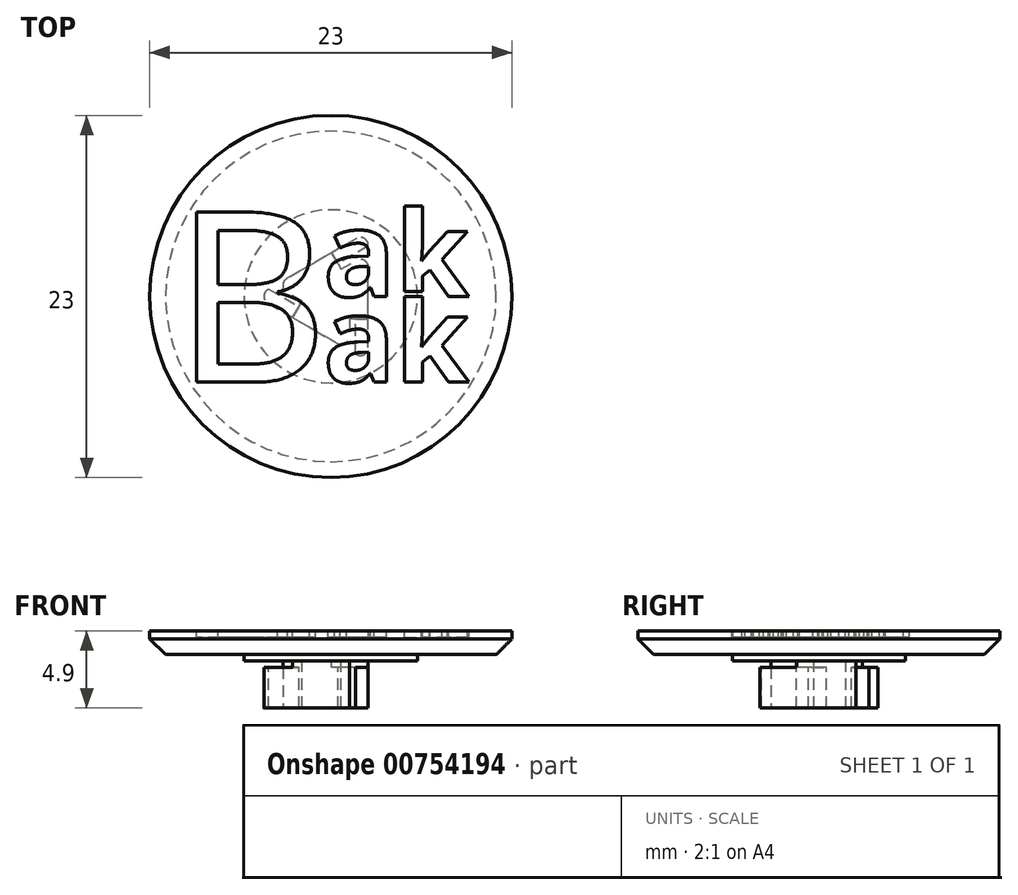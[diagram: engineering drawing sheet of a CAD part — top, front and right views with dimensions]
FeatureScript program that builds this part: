
annotation { "Feature Type Name" : "Feature", "Feature Type Description" : "" }
export const myFeature = defineFeature(function(context is Context, id is Id, definition is map)
    precondition{}
    {
        {
            var Q0;
            Q0=qCreatedBy(makeId("Front.planeOp"),FACE);
            var sketch = newSketch(context, id + "F0", { "sketchPlane" : qUnion([Q0])});
            skLineSegment(sketch, "E0", {"start": v(-4, 5.4) * mm, "end": v(-4, 1.9) * mm});
            skLineSegment(sketch, "E1", {"start": v(-4, 1.9) * mm, "end": v(-5.5, 1.9) * mm});
            skLineSegment(sketch, "E2", {"start": v(-5.5, 1.9) * mm, "end": v(-5.5, 1.5) * mm});
            skLineSegment(sketch, "E3", {"start": v(-5.5, 1.5) * mm, "end": v(-10.5, 1.5) * mm});
            skLineSegment(sketch, "E4", {"start": v(-10.5, 1.5) * mm, "end": v(-11.5, 0.5) * mm});
            skLineSegment(sketch, "E5", {"start": v(-11.5, 0.5) * mm, "end": v(-11.5, 0) * mm});
            skLineSegment(sketch, "E6", {"start": v(-11.5, 0) * mm, "end": v(0, 0) * mm});
            skLineSegment(sketch, "E7", {"start": v(0, 0) * mm, "end": v(0, 5.4) * mm});
            skLineSegment(sketch, "E8", {"start": v(0, 5.4) * mm, "end": v(-4, 5.4) * mm});
            skSolve(sketch);
        }
        {
            var Q0;
            Q0=makeQuery(id+"F0.imprint","IMPRINT",FACE,{"disambiguationData":[TD([[makeQuery(id+"F0.imprint","IMPRINT",EDGE,{"derivedFrom":sQuery(id+"F0.wireOp",EDGE,"E0")}),1.0]])]});
            var Q1;
            Q1=sQuery(id+"F0.wireOp",EDGE,"E7");
            revolve(context, id + "F1", {"surfaceOperationType" : NewSurfaceOperationType.NEW, "entities" : qUnion([Q0]), "axis" : qUnion([Q1]), "revolveType" : RevolveType.FULL});
        }
        {
            var Q0;
            Q0=makeQuery(id+"F1.opRevolve","SWEPT_FACE",FACE,{"disambiguationData":[OSD([sQuery(id+"F0.wireOp",EDGE,"E8")])]});
            var sketch = newSketch(context, id + "F2", { "sketchPlane" : qUnion([Q0])});
            skCircle(sketch, "E9.cCircle", {"center": v(0, 0) * mm, "radius": 4 * mm, "construction": true});
            skLineSegment(sketch, "E9.0", {"start": v(0, 4) * mm, "end": v(4, 0) * mm});
            skLineSegment(sketch, "E9.1", {"start": v(4, 0) * mm, "end": v(0, -4) * mm});
            skLineSegment(sketch, "E9.2", {"start": v(0, -4) * mm, "end": v(-4, 0) * mm});
            skLineSegment(sketch, "E9.3", {"start": v(-4, 0) * mm, "end": v(0, 4) * mm});
            skSolve(sketch);
        }
        {
            var Q0;
            {var subQ0=sQuery(id+"F2.wireOp",EDGE,"E9.3");Q0=makeQuery(id+"F2.imprint","IMPRINT",FACE,{"disambiguationData":[TD([[makeQuery(id+"F2.imprint","IMPRINT",EDGE,{"derivedFrom":subQ0}),1.0]])]});}
            var Q1;
            {var subQ0=sQuery(id+"F2.wireOp",EDGE,"E9.2");Q1=makeQuery(id+"F2.imprint","IMPRINT",FACE,{"disambiguationData":[TD([[makeQuery(id+"F2.imprint","IMPRINT",EDGE,{"derivedFrom":subQ0}),1.0]])]});}
            var Q2;
            {var subQ0=sQuery(id+"F2.wireOp",EDGE,"E9.1");Q2=makeQuery(id+"F2.imprint","IMPRINT",FACE,{"disambiguationData":[TD([[makeQuery(id+"F2.imprint","IMPRINT",EDGE,{"derivedFrom":subQ0}),1.0]])]});}
            var Q3;
            {var subQ0=sQuery(id+"F2.wireOp",EDGE,"E9.0");Q3=makeQuery(id+"F2.imprint","IMPRINT",FACE,{"disambiguationData":[TD([[makeQuery(id+"F2.imprint","IMPRINT",EDGE,{"derivedFrom":subQ0}),1.0]])]});}
            var Q4;
            Q4=makeQuery(id+"F1.opRevolve","SWEPT_FACE",FACE,{"disambiguationData":[OSD([sQuery(id+"F0.wireOp",EDGE,"E1")])]});
            extrude(context, id + "F3", {"entities" : qUnion([Q0, Q1, Q2, Q3]), "operationType" : NewBodyOperationType.REMOVE, "endBound" : BoundingType.UP_TO_SURFACE, "oppositeDirection" : true, "depth" : 25 * mm, "endBoundEntityFace" : qUnion([Q4]), "offsetDistance" : 25 * mm});
        }
        {
            var Q0;
            Q0=qCreatedBy(makeId("Top.planeOp"),FACE);
            var sketch = newSketch(context, id + "F4", { "sketchPlane" : qUnion([Q0])});
            skLineSegment(sketch, "E10", {"start": v(0, 61.35) * mm, "end": v(0, -45.77) * mm});
            skSolve(sketch);
        }
        {
            var Q0;
            Q0=makeQuery(id+"F1.opRevolve","SWEPT_BODY",BODY,{"disambiguationData":[OSD([sQuery(id+"F0.wireOp",EDGE,"E0"),sQuery(id+"F0.wireOp",EDGE,"E1"),sQuery(id+"F0.wireOp",EDGE,"E2"),sQuery(id+"F0.wireOp",EDGE,"E3"),sQuery(id+"F0.wireOp",EDGE,"E4"),sQuery(id+"F0.wireOp",EDGE,"E5"),sQuery(id+"F0.wireOp",EDGE,"E6"),sQuery(id+"F0.wireOp",EDGE,"E7"),sQuery(id+"F0.wireOp",EDGE,"E8")])]});
            var Q1;
            Q1=sQuery(id+"F4.wireOp",EDGE,"E10");
            transform(context, id + "F5", {"entities" : qUnion([Q0]), "transformType" : TransformType.ROTATION, "transformAxis" : qUnion([Q1]), "angle" : 180 * degree, "makeCopy" : false});
        }
        {
            var Q0;
            Q0=makeQuery(id+"F1.opRevolve","SWEPT_FACE",FACE,{"disambiguationData":[OSD([sQuery(id+"F0.wireOp",EDGE,"E6")])]});
            var sketch = newSketch(context, id + "F6", { "sketchPlane" : qUnion([Q0])});
            skLineSegment(sketch, "E11.bottom", {"start": v(-11.93, 11.93) * mm, "end": v(11.93, 11.93) * mm, "construction": true});
            skLineSegment(sketch, "E11.top", {"start": v(-11.93, -11.93) * mm, "end": v(11.93, -11.93) * mm, "construction": true});
            skLineSegment(sketch, "E11.left", {"start": v(-11.93, 11.93) * mm, "end": v(-11.93, -11.93) * mm, "construction": true});
            skLineSegment(sketch, "E11.right", {"start": v(11.93, 11.93) * mm, "end": v(11.93, -11.93) * mm, "construction": true});
            skLineSegment(sketch, "E12", {"start": v(-11.93, 11.93) * mm, "end": v(11.93, -11.93) * mm, "construction": true});
            skLineSegment(sketch, "E13", {"start": v(11.93, 11.93) * mm, "end": v(-11.93, -11.93) * mm, "construction": true});
            skText(sketch, "E14", { "text": "B\n", "fontName": "NotoSans-Regular.ttf"});
            skText(sketch, "E15", { "text": "ak", "fontName": "OpenSans-Bold.ttf"});
            skText(sketch, "E16", { "text": "ak", "fontName": "OpenSans-Bold.ttf"});
            const initialGuessF6  = {"E14": [-0.01, -0.00545, 1, 0, 0.0109], "E15": [-0.00048, 0, 1, 0, 0.00545], "E16": [-0.00048, -0.00545, 1, 0, 0.00545]};
            skSetInitialGuess(sketch, initialGuessF6);
            skSolve(sketch);
        }
        {
            var Q0;
            Q0=makeQuery(id+"F6.imprint","IMPRINT",FACE,{"disambiguationData":[TD([[makeQuery(id+"F6.imprint","IMPRINT",EDGE,{"derivedFrom":sQuery(id+"F6.wireOp",EDGE,"E14.sketch_text.stroke-0")}),-1.0]])]});
            var Q1;
            Q1=makeQuery(id+"F6.imprint","IMPRINT",FACE,{"disambiguationData":[TD([[makeQuery(id+"F6.imprint","IMPRINT",EDGE,{"derivedFrom":sQuery(id+"F6.wireOp",EDGE,"E15.sketch_text.stroke-0")}),-1.0]])]});
            var Q2;
            Q2=makeQuery(id+"F6.imprint","IMPRINT",FACE,{"disambiguationData":[TD([[makeQuery(id+"F6.imprint","IMPRINT",EDGE,{"derivedFrom":sQuery(id+"F6.wireOp",EDGE,"E15.sketch_text.stroke-25")}),-1.0]])]});
            var Q3;
            {var subQ0=sQuery(id+"F6.wireOp",EDGE,"E15.sketch_text.stroke-34");Q3=makeQuery(id+"F6.imprint","IMPRINT",FACE,{"disambiguationData":[TD([[makeQuery(id+"F6.imprint","IMPRINT",EDGE,{"derivedFrom":subQ0}),1.0]])]});}
            var Q4;
            Q4=makeQuery(id+"F6.imprint","IMPRINT",FACE,{"disambiguationData":[TD([[makeQuery(id+"F6.imprint","IMPRINT",EDGE,{"derivedFrom":sQuery(id+"F6.wireOp",EDGE,"E16.sketch_text.stroke-0")}),-1.0]])]});
            extrude(context, id + "F7", {"entities" : qUnion([Q0, Q1, Q2, Q3, Q4]), "operationType" : NewBodyOperationType.REMOVE, "oppositeDirection" : true, "depth" : .4 * mm, "offsetDistance" : 25 * mm});
        }
        {
            var Q0;
            Q0=makeQuery(id+"F1.opRevolve","SWEPT_FACE",FACE,{"disambiguationData":[OSD([sQuery(id+"F0.wireOp",EDGE,"E8")])]});
            var Q1;
            {var subQ0=sQuery(id+"F0.wireOp",EDGE,"E1");Q1=makeQuery(id+"F3.boolean.opBoolean","MERGE",FACE,{"derivedFrom":[makeQuery(id+"F1.opRevolve","SWEPT_FACE",FACE,{"disambiguationData":[OSD([subQ0])]}),makeQuery(id+"F3.opExtrude","CAP_FACE",FACE,{"disambiguationData":[OSD([subQ0]),OD(0.0)],"isStart":false}),makeQuery(id+"F3.opExtrude","CAP_FACE",FACE,{"disambiguationData":[OSD([subQ0]),OD(1.0)],"isStart":false}),makeQuery(id+"F3.opExtrude","CAP_FACE",FACE,{"disambiguationData":[OSD([subQ0]),OD(2.0)],"isStart":false}),makeQuery(id+"F3.opExtrude","CAP_FACE",FACE,{"disambiguationData":[OSD([subQ0]),OD(3.0)],"isStart":false})]});}
            extrude(context, id + "F8", {"entities" : qUnion([Q0]), "operationType" : NewBodyOperationType.REMOVE, "endBound" : BoundingType.UP_TO_SURFACE, "oppositeDirection" : true, "depth" : 25 * mm, "endBoundEntityFace" : qUnion([Q1]), "offsetDistance" : 25 * mm});
        }
        {
            var Q0;
            {var subQ0=sQuery(id+"F0.wireOp",EDGE,"E1");Q0=makeQuery(id+"F8.boolean.opBoolean","MERGE",FACE,{"derivedFrom":[makeQuery(id+"F3.boolean.opBoolean","MERGE",FACE,{"derivedFrom":[makeQuery(id+"F1.opRevolve","SWEPT_FACE",FACE,{"disambiguationData":[OSD([subQ0])]}),makeQuery(id+"F3.opExtrude","CAP_FACE",FACE,{"disambiguationData":[OSD([subQ0]),OD(0.0)],"isStart":false}),makeQuery(id+"F3.opExtrude","CAP_FACE",FACE,{"disambiguationData":[OSD([subQ0]),OD(1.0)],"isStart":false}),makeQuery(id+"F3.opExtrude","CAP_FACE",FACE,{"disambiguationData":[OSD([subQ0]),OD(2.0)],"isStart":false}),makeQuery(id+"F3.opExtrude","CAP_FACE",FACE,{"disambiguationData":[OSD([subQ0]),OD(3.0)],"isStart":false})]}),makeQuery(id+"F8.opExtrude","CAP_FACE",FACE,{"disambiguationData":[OSD([subQ0])],"isStart":false})]});}
            var sketch = newSketch(context, id + "F9", { "sketchPlane" : qUnion([Q0])});
            skCircle(sketch, "E17.cCircle", {"center": v(0, 0) * mm, "radius": 4.75 * mm, "construction": true});
            skLineSegment(sketch, "E17.0", {"start": v(-4.75, 0) * mm, "end": v(2.37, 4.11) * mm});
            skLineSegment(sketch, "E17.1", {"start": v(2.37, 4.11) * mm, "end": v(2.37, -4.11) * mm});
            skLineSegment(sketch, "E17.2", {"start": v(2.38, -4.11) * mm, "end": v(-4.75, 0) * mm});
            skLineSegment(sketch, "E18", {"start": v(1.57, 3.65) * mm, "end": v(1.57, 1.42) * mm});
            skLineSegment(sketch, "E19", {"start": v(1.57, 1.42) * mm, "end": v(1.17, 1.42) * mm});
            skLineSegment(sketch, "E20", {"start": v(1.17, 1.42) * mm, "end": v(1.17, 3.42) * mm});
            skLineSegment(sketch, "E21.1.0", {"start": v(-1.82, 0.3) * mm, "end": v(-3.55, -0.7) * mm});
            skLineSegment(sketch, "E21.1.1", {"start": v(-2.02, 0.65) * mm, "end": v(-1.82, 0.3) * mm});
            skLineSegment(sketch, "E21.1.2", {"start": v(-3.95, -0.46) * mm, "end": v(-2.02, 0.65) * mm});
            skLineSegment(sketch, "E21.2.0", {"start": v(0.64, -1.73) * mm, "end": v(2.37, -2.73) * mm});
            skLineSegment(sketch, "E21.2.1", {"start": v(0.44, -2.07) * mm, "end": v(0.64, -1.73) * mm});
            skLineSegment(sketch, "E21.2.2", {"start": v(2.38, -3.19) * mm, "end": v(0.44, -2.07) * mm});
            skSolve(sketch);
        }
        {
            var Q0;
            {var subQ1=sQuery(id+"F9.wireOp",EDGE,"E18");Q0=makeQuery(id+"F9.imprint","IMPRINT",FACE,{"disambiguationData":[TD([[makeQuery(id+"F9.imprint","IMPRINT",EDGE,{"derivedFrom":subQ1}),1.0]])]});}
            extrude(context, id + "F10", {"entities" : qUnion([Q0]), "operationType" : NewBodyOperationType.ADD, "depth" : 3 * mm, "offsetDistance" : 25 * mm});
        }
        {
            var Q0;
            {var subQ0=sQuery(id+"F0.wireOp",EDGE,"E1");Q0=makeQuery(id+"F8.boolean.opBoolean","MERGE",FACE,{"derivedFrom":[makeQuery(id+"F3.boolean.opBoolean","MERGE",FACE,{"derivedFrom":[makeQuery(id+"F1.opRevolve","SWEPT_FACE",FACE,{"disambiguationData":[OSD([subQ0])]}),makeQuery(id+"F3.opExtrude","CAP_FACE",FACE,{"disambiguationData":[OSD([subQ0]),OD(0.0)],"isStart":false}),makeQuery(id+"F3.opExtrude","CAP_FACE",FACE,{"disambiguationData":[OSD([subQ0]),OD(1.0)],"isStart":false}),makeQuery(id+"F3.opExtrude","CAP_FACE",FACE,{"disambiguationData":[OSD([subQ0]),OD(2.0)],"isStart":false}),makeQuery(id+"F3.opExtrude","CAP_FACE",FACE,{"disambiguationData":[OSD([subQ0]),OD(3.0)],"isStart":false})]}),makeQuery(id+"F8.opExtrude","CAP_FACE",FACE,{"disambiguationData":[OSD([subQ0])],"isStart":false})]});}
            var sketch = newSketch(context, id + "F11", { "sketchPlane" : qUnion([Q0])});
            skLineSegment(sketch, "E22", {"start": v(1.57, 1.42) * mm, "end": v(2.37, 1.42) * mm});
            skLineSegment(sketch, "E23", {"start": v(0.44, -2.07) * mm, "end": v(0.04, -2.77) * mm});
            skLineSegment(sketch, "E24", {"start": v(-2.02, 0.65) * mm, "end": v(-2.42, 1.35) * mm});
            skSolve(sketch);
        }
        {
            var Q0;
            {var subQ0=sQuery(id+"F11.wireOp",EDGE,"E24");Q0=makeQuery(id+"F11.imprint","IMPRINT",FACE,{"disambiguationData":[TD([[makeQuery(id+"F11.imprint","IMPRINT",EDGE,{"derivedFrom":subQ0}),1.0]])]});}
            var Q1;
            {var subQ0=sQuery(id+"F11.wireOp",EDGE,"E22");Q1=makeQuery(id+"F11.imprint","IMPRINT",FACE,{"disambiguationData":[TD([[makeQuery(id+"F11.imprint","IMPRINT",EDGE,{"derivedFrom":subQ0}),1.0]])]});}
            var Q2;
            {var subQ0=sQuery(id+"F11.wireOp",EDGE,"E23");Q2=makeQuery(id+"F11.imprint","IMPRINT",FACE,{"disambiguationData":[TD([[makeQuery(id+"F11.imprint","IMPRINT",EDGE,{"derivedFrom":subQ0}),1.0]])]});}
            extrude(context, id + "F12", {"entities" : qUnion([Q0, Q1, Q2]), "operationType" : NewBodyOperationType.REMOVE, "depth" : .4 * mm, "offsetDistance" : 25 * mm});
        }
        {
            var Q0;
            Q0=makeQuery(id+"F10.opExtrude","SWEPT_EDGE",EDGE,{"disambiguationData":[OSD([sQuery(id+"F9.wireOp",EDGE,"E17.0"),sQuery(id+"F9.wireOp",EDGE,"E17.1")])]});
            var Q1;
            Q1=makeQuery(id+"F10.opExtrude","SWEPT_EDGE",EDGE,{"disambiguationData":[OSD([sQuery(id+"F9.wireOp",EDGE,"E17.0"),sQuery(id+"F9.wireOp",EDGE,"E17.2")])]});
            var Q2;
            Q2=makeQuery(id+"F10.opExtrude","SWEPT_EDGE",EDGE,{"disambiguationData":[OSD([sQuery(id+"F9.wireOp",EDGE,"E17.1"),sQuery(id+"F9.wireOp",EDGE,"E17.2")])]});
            var Q3;
            Q3=makeQuery(id+"F10.opExtrude","SWEPT_EDGE",EDGE,{"disambiguationData":[OSD([sQuery(id+"F9.wireOp",EDGE,"E17.2"),sQuery(id+"F9.wireOp",EDGE,"E21.1.0")])]});
            var Q4;
            Q4=makeQuery(id+"F10.opExtrude","SWEPT_EDGE",EDGE,{"disambiguationData":[OSD([sQuery(id+"F9.wireOp",EDGE,"E17.1"),sQuery(id+"F9.wireOp",EDGE,"E21.2.0")])]});
            var Q5;
            Q5=makeQuery(id+"F10.opExtrude","SWEPT_EDGE",EDGE,{"disambiguationData":[OSD([sQuery(id+"F9.wireOp",EDGE,"E17.0"),sQuery(id+"F9.wireOp",EDGE,"E20")])]});
            fillet(context, id + "F13", {"entities" : qUnion([Q0, Q1, Q2, Q3, Q4, Q5]), "radius" : .5 * mm, "tangentPropagation" : true, "allowEdgeOverflow" : false});
        }
    });
